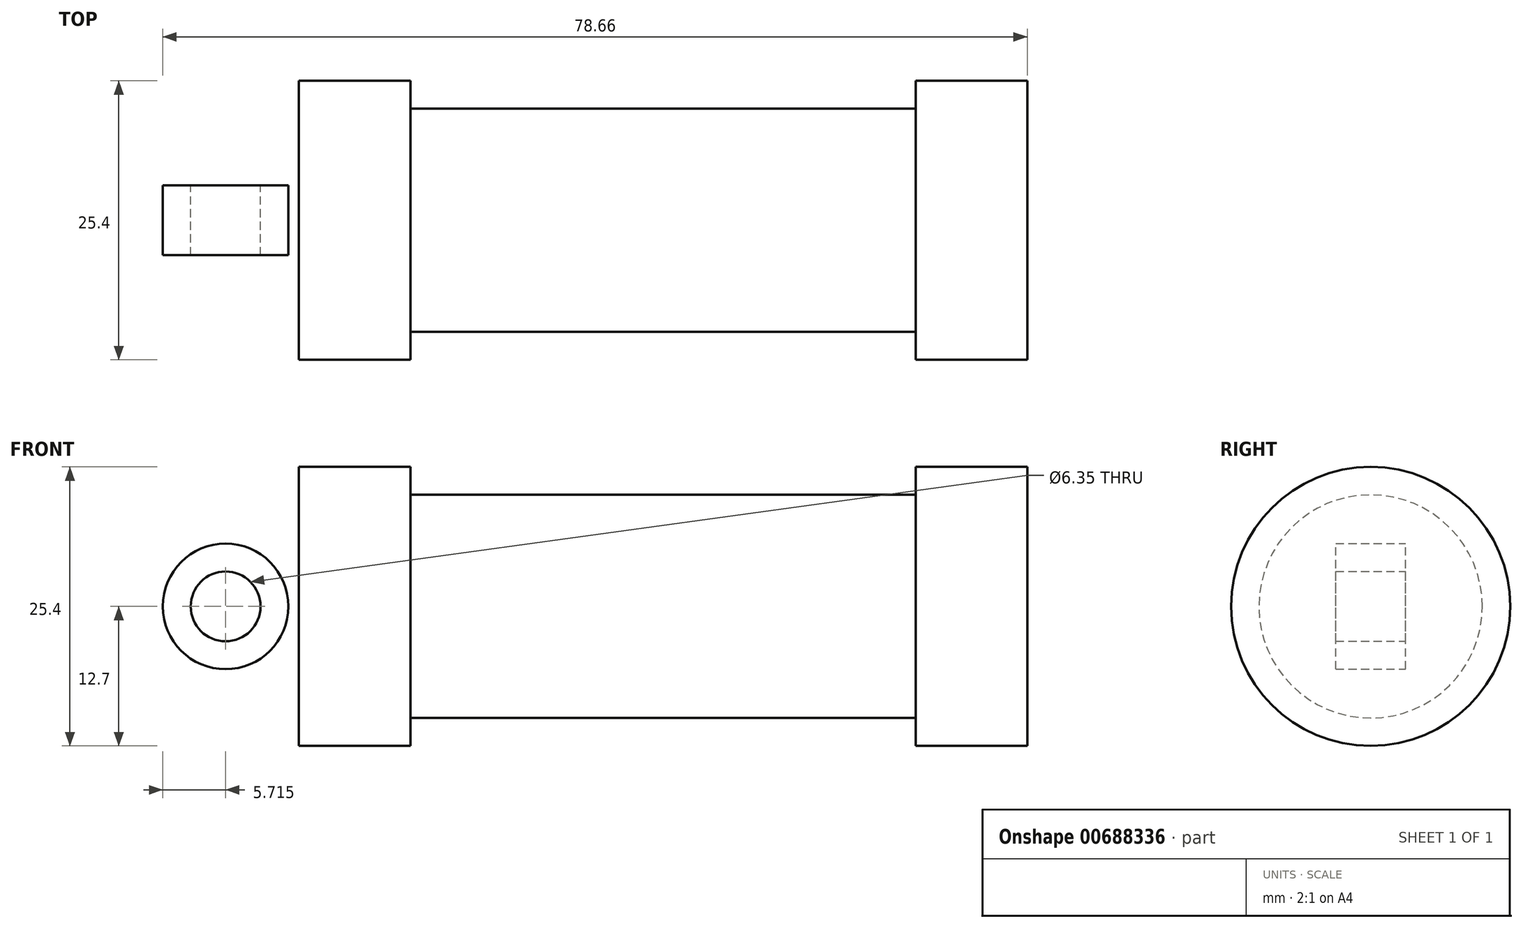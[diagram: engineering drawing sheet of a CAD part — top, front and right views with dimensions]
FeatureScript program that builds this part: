
annotation { "Feature Type Name" : "Feature", "Feature Type Description" : "" }
export const myFeature = defineFeature(function(context is Context, id is Id, definition is map)
    precondition{}
    {
        {
            var Q0;
            Q0=qCreatedBy(makeId("Front.planeOp"),FACE);
            var sketch = newSketch(context, id + "F0", { "sketchPlane" : qUnion([Q0])});
            skLineSegment(sketch, "E0", {"start": v(0, 0) * mm, "end": v(0, 12.7) * mm});
            skLineSegment(sketch, "E1", {"start": v(0, 12.7) * mm, "end": v(10.16, 12.7) * mm});
            skLineSegment(sketch, "E2", {"start": v(10.16, 12.7) * mm, "end": v(10.16, 10.16) * mm});
            skLineSegment(sketch, "E3", {"start": v(10.16, 10.16) * mm, "end": v(56.13, 10.16) * mm});
            skLineSegment(sketch, "E4", {"start": v(56.13, 10.16) * mm, "end": v(56.13, 12.7) * mm});
            skLineSegment(sketch, "E5", {"start": v(56.13, 12.7) * mm, "end": v(66.3, 12.7) * mm});
            skLineSegment(sketch, "E6", {"start": v(66.3, 12.7) * mm, "end": v(66.3, 0) * mm});
            skLineSegment(sketch, "E7", {"start": v(66.3, 0) * mm, "end": v(0, 0) * mm});
            skLineSegment(sketch, "E8", {"start": v(5.84, 15.24) * mm, "end": v(-0.5, 15.24) * mm});
            skLineSegment(sketch, "E9", {"start": v(-0.5, 15.24) * mm, "end": v(-10.88, 3.85) * mm});
            skLineSegment(sketch, "E10", {"start": v(0, 0) * mm, "end": v(-6.65, 0) * mm});
            skCircle(sketch, "E11", {"center": v(-6.65, 0) * mm, "radius": 5.72 * mm});
            skCircle(sketch, "E12", {"center": v(-6.65, 0) * mm, "radius": 3.18 * mm});
            skLineSegment(sketch, "E13", {"start": v(5.84, 15.24) * mm, "end": v(5.84, -9.4) * mm});
            skLineSegment(sketch, "E14", {"start": v(5.84, -9.4) * mm, "end": v(-8.18, -5.5) * mm});
            skSolve(sketch);
        }
        {
            var Q0;
            {var subQ0=sQuery(id+"F0.wireOp",EDGE,"E0");Q0=makeQuery(id+"F0.imprint","IMPRINT",FACE,{"disambiguationData":[TD([[makeQuery(id+"F0.imprint","IMPRINT",EDGE,{"derivedFrom":subQ0}),-1.0]])]});}
            var Q1;
            {var subQ0=sQuery(id+"F0.wireOp",EDGE,"E2");Q1=makeQuery(id+"F0.imprint","IMPRINT",FACE,{"disambiguationData":[TD([[makeQuery(id+"F0.imprint","IMPRINT",EDGE,{"derivedFrom":subQ0}),-1.0]])]});}
            var Q2;
            Q2=sQuery(id+"F0.wireOp",EDGE,"E7");
            revolve(context, id + "F1", {"entities" : qUnion([Q0, Q1]), "axis" : qUnion([Q2]), "revolveType" : RevolveType.FULL});
        }
        {
            var Q0;
            {var subQ5=sQuery(id+"F0.wireOp",EDGE,"E12");Q0=makeQuery(id+"F0.imprint","IMPRINT",FACE,{"disambiguationData":[TD([[makeQuery(id+"F0.imprint","IMPRINT",EDGE,{"derivedFrom":subQ5}),-1.0]])]});}
            extrude(context, id + "F2", {"entities" : qUnion([Q0]), "operationType" : NewBodyOperationType.ADD, "endBound" : BoundingType.SYMMETRIC, "depth" : 6.35 * mm, "offsetDistance" : 25.4 * mm});
        }
    });
